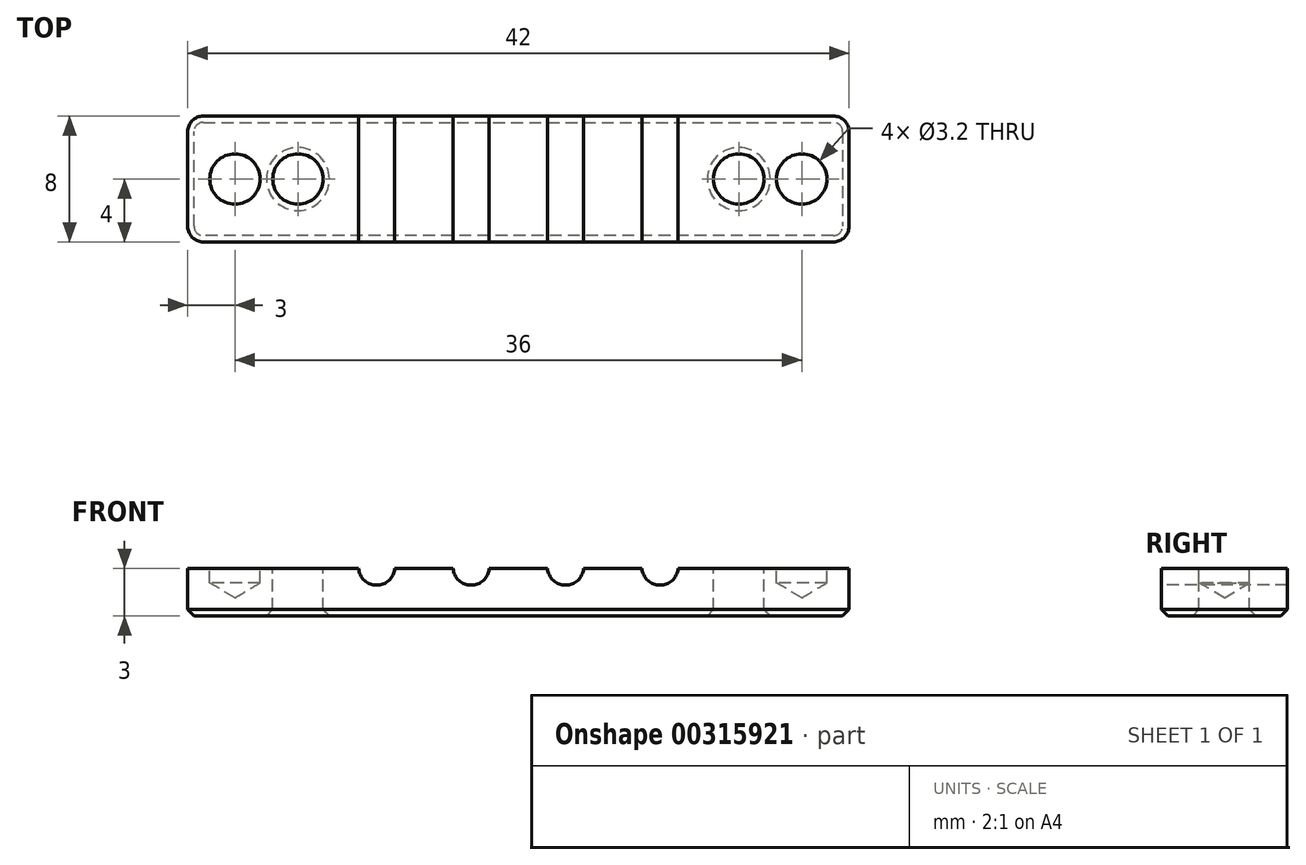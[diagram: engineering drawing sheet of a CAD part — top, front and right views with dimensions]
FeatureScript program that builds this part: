
annotation { "Feature Type Name" : "Feature", "Feature Type Description" : "" }
export const myFeature = defineFeature(function(context is Context, id is Id, definition is map)
    precondition{}
    {
        {
            var Q0;
            Q0=qCreatedBy(makeId("Top.planeOp"),FACE);
            var sketch = newSketch(context, id + "F0", { "sketchPlane" : qUnion([Q0])});
            skLineSegment(sketch, "E0.bottom", {"start": v(3, 4) * mm, "end": v(-3, 4) * mm});
            skLineSegment(sketch, "E0.top", {"start": v(3, -4) * mm, "end": v(-3, -4) * mm});
            skLineSegment(sketch, "E0.left", {"start": v(3, 4) * mm, "end": v(3, -4) * mm});
            skLineSegment(sketch, "E0.right", {"start": v(-3, 4) * mm, "end": v(-3, -4) * mm});
            skPoint(sketch, "E0.middle", {"position": v(0, 0) * mm});
            skLineSegment(sketch, "E1.bottom", {"start": v(39, 4) * mm, "end": v(33, 4) * mm});
            skLineSegment(sketch, "E1.top", {"start": v(39, -4) * mm, "end": v(33, -4) * mm});
            skLineSegment(sketch, "E1.left", {"start": v(39, 4) * mm, "end": v(39, -4) * mm});
            skLineSegment(sketch, "E1.right", {"start": v(33, 4) * mm, "end": v(33, -4) * mm});
            skPoint(sketch, "E1.middle", {"position": v(36, 0) * mm});
            skLineSegment(sketch, "E2", {"start": v(3, 4) * mm, "end": v(33, 4) * mm});
            skLineSegment(sketch, "E3", {"start": v(3, -4) * mm, "end": v(33, -4) * mm});
            skLineSegment(sketch, "E4", {"start": v(9, 4) * mm, "end": v(9, -4) * mm, "construction": true});
            skLineSegment(sketch, "E5.direction1", {"start": v(9, -4) * mm, "end": v(15, -4) * mm, "construction": true});
            skPoint(sketch, "E6", {"position": v(4, 0) * mm});
            skPoint(sketch, "E6.positionSnap0", {"position": v(3, 0) * mm});
            skPoint(sketch, "E7", {"position": v(32, 0) * mm});
            skPoint(sketch, "E7.positionSnap0", {"position": v(33, 0) * mm});
            skLineSegment(sketch, "E8.0.1.0", {"start": v(15, 4) * mm, "end": v(15, -4) * mm, "construction": true});
            skLineSegment(sketch, "E8.0.2.0", {"start": v(21, 4) * mm, "end": v(21, -4) * mm, "construction": true});
            skLineSegment(sketch, "E8.0.3.0", {"start": v(27, 4) * mm, "end": v(27, -4) * mm, "construction": true});
            skSolve(sketch);
        }
        {
            var Q0;
            Q0=makeQuery(id+"F0.imprint","IMPRINT",FACE,{"disambiguationData":[TD([[makeQuery(id+"F0.imprint","IMPRINT",EDGE,{"derivedFrom":sQuery(id+"F0.wireOp",EDGE,"E0.bottom")}),1.0]])]});
            var Q1;
            Q1=makeQuery(id+"F0.imprint","IMPRINT",FACE,{"disambiguationData":[TD([[makeQuery(id+"F0.imprint","IMPRINT",EDGE,{"derivedFrom":sQuery(id+"F0.wireOp",EDGE,"E0.left")}),1.0]])]});
            var Q2;
            Q2=makeQuery(id+"F0.imprint","IMPRINT",FACE,{"disambiguationData":[TD([[makeQuery(id+"F0.imprint","IMPRINT",EDGE,{"derivedFrom":sQuery(id+"F0.wireOp",EDGE,"E1.bottom")}),1.0]])]});
            extrude(context, id + "F1", {"entities" : qUnion([Q0, Q1, Q2]), "oppositeDirection" : true, "depth" : 3.1 * mm});
        }
        {
            var Q0;
            Q0=sQuery(id+"F0.wireOp",VERTEX,"E6");
            var Q1;
            Q1=sQuery(id+"F0.wireOp",VERTEX,"E7");
            var Q2;
            Q2=makeQuery(id+"F1.opExtrude","SWEPT_BODY",BODY,{"disambiguationData":[OSD([sQuery(id+"F0.wireOp",EDGE,"E0.bottom"),sQuery(id+"F0.wireOp",EDGE,"E0.top"),sQuery(id+"F0.wireOp",EDGE,"E0.right"),sQuery(id+"F0.wireOp",EDGE,"E1.bottom"),sQuery(id+"F0.wireOp",EDGE,"E1.top"),sQuery(id+"F0.wireOp",EDGE,"E1.left"),sQuery(id+"F0.wireOp",EDGE,"E2"),sQuery(id+"F0.wireOp",EDGE,"E3")])]});
            hole(context, id + "F2", {"style" : HoleStyle.SIMPLE, "endStyle" : HoleEndStyle.THROUGH, "holeDiameter" : 3.2 * mm, "tappedDepth" : 12 * mm, "tapClearance" : 3, "locations" : qUnion([Q0, Q1]), "scope" : qUnion([Q2])});
        }
        {
            var Q0;
            Q0=sQuery(id+"F0.wireOp",VERTEX,"E0.middle");
            var Q1;
            Q1=sQuery(id+"F0.wireOp",VERTEX,"E1.middle");
            var Q2;
            Q2=makeQuery(id+"F1.opExtrude","SWEPT_BODY",BODY,{"disambiguationData":[OSD([sQuery(id+"F0.wireOp",EDGE,"E0.bottom"),sQuery(id+"F0.wireOp",EDGE,"E0.top"),sQuery(id+"F0.wireOp",EDGE,"E0.right"),sQuery(id+"F0.wireOp",EDGE,"E1.bottom"),sQuery(id+"F0.wireOp",EDGE,"E1.top"),sQuery(id+"F0.wireOp",EDGE,"E1.left"),sQuery(id+"F0.wireOp",EDGE,"E2"),sQuery(id+"F0.wireOp",EDGE,"E3")])]});
            hole(context, id + "F3", {"style" : HoleStyle.SIMPLE, "endStyle" : HoleEndStyle.BLIND, "holeDiameter" : 3.2 * mm, "holeDepth" : 1 * mm, "tappedDepth" : 12 * mm, "tapClearance" : 3, "locations" : qUnion([Q0, Q1]), "scope" : qUnion([Q2])});
        }
        {
            var Q0;
            {var subQ0=sQuery(id+"F0.wireOp",EDGE,"E3");var subQ1=sQuery(id+"F0.wireOp",EDGE,"E1.top");var subQ2=sQuery(id+"F0.wireOp",EDGE,"E0.top");Q0=makeQuery(id+"FaaVOSY5iOmgxNq_1.boolean.opBoolean","MERGE",FACE,{"derivedFrom":[makeQuery(id+"F1.opExtrude","SWEPT_FACE",FACE,{"disambiguationData":[OSD([subQ2,subQ1,subQ0])]}),makeQuery(id+"FaaVOSY5iOmgxNq_1.opExtrude","SWEPT_FACE",FACE,{"disambiguationData":[OSD([subQ2,subQ1,subQ0])]})]});}
            var sketch = newSketch(context, id + "F4", { "sketchPlane" : qUnion([Q0])});
            skPoint(sketch, "E9", {"position": v(9, 0) * mm});
            skPoint(sketch, "E10.1.0.0", {"position": v(15, 0) * mm});
            skLineSegment(sketch, "E10.direction1", {"start": v(9, 0) * mm, "end": v(15, 0) * mm, "construction": true});
            skPoint(sketch, "E11.0.2.0", {"position": v(21, 0) * mm});
            skPoint(sketch, "E11.0.3.0", {"position": v(27, 0) * mm});
            skSolve(sketch);
        }
        {
            var Q0;
            Q0=sQuery(id+"F4.wireOp",VERTEX,"E9");
            var Q1;
            Q1=sQuery(id+"F4.wireOp",VERTEX,"E10.1.0.0");
            var Q2;
            Q2=sQuery(id+"F4.wireOp",VERTEX,"E11.0.2.0");
            var Q3;
            Q3=sQuery(id+"F4.wireOp",VERTEX,"E11.0.3.0");
            var Q4;
            Q4=makeQuery(id+"F1.opExtrude","SWEPT_BODY",BODY,{"disambiguationData":[OSD([sQuery(id+"F0.wireOp",EDGE,"E0.bottom"),sQuery(id+"F0.wireOp",EDGE,"E0.top"),sQuery(id+"F0.wireOp",EDGE,"E0.right"),sQuery(id+"F0.wireOp",EDGE,"E1.bottom"),sQuery(id+"F0.wireOp",EDGE,"E1.top"),sQuery(id+"F0.wireOp",EDGE,"E1.left"),sQuery(id+"F0.wireOp",EDGE,"E2"),sQuery(id+"F0.wireOp",EDGE,"E3")])]});
            hole(context, id + "F5", {"style" : HoleStyle.SIMPLE, "endStyle" : HoleEndStyle.THROUGH, "holeDiameter" : 2.3 * mm, "tappedDepth" : 12 * mm, "tapClearance" : 3, "locations" : qUnion([Q0, Q1, Q2, Q3]), "scope" : qUnion([Q4])});
        }
        {
            var Q0;
            Q0=makeQuery(id+"F1.opExtrude","SWEPT_EDGE",EDGE,{"disambiguationData":[OSD([sQuery(id+"F0.wireOp",EDGE,"E0.top"),sQuery(id+"F0.wireOp",EDGE,"E0.right")])]});
            var Q1;
            Q1=makeQuery(id+"F1.opExtrude","SWEPT_EDGE",EDGE,{"disambiguationData":[OSD([sQuery(id+"F0.wireOp",EDGE,"E1.top"),sQuery(id+"F0.wireOp",EDGE,"E1.left")])]});
            var Q2;
            Q2=makeQuery(id+"F1.opExtrude","SWEPT_EDGE",EDGE,{"disambiguationData":[OSD([sQuery(id+"F0.wireOp",EDGE,"E1.bottom"),sQuery(id+"F0.wireOp",EDGE,"E1.left")])]});
            var Q3;
            Q3=makeQuery(id+"F1.opExtrude","SWEPT_EDGE",EDGE,{"disambiguationData":[OSD([sQuery(id+"F0.wireOp",EDGE,"E0.bottom"),sQuery(id+"F0.wireOp",EDGE,"E0.right")])]});
            fillet(context, id + "F6", {"entities" : qUnion([Q0, Q1, Q2, Q3]), "radius" : 1 * mm, "tangentPropagation" : true, "allowEdgeOverflow" : false});
        }
        {
            var Q0;
            Q0=makeQuery(id+"F1.opExtrude","CAP_FACE",FACE,{"disambiguationData":[OSD([sQuery(id+"F0.wireOp",EDGE,"E0.bottom"),sQuery(id+"F0.wireOp",EDGE,"E0.top"),sQuery(id+"F0.wireOp",EDGE,"E0.right"),sQuery(id+"F0.wireOp",EDGE,"E1.bottom"),sQuery(id+"F0.wireOp",EDGE,"E1.top"),sQuery(id+"F0.wireOp",EDGE,"E1.left"),sQuery(id+"F0.wireOp",EDGE,"E2"),sQuery(id+"F0.wireOp",EDGE,"E3")])],"isStart":false});
            chamfer(context, id + "F7", {"entities" : qUnion([Q0]), "width" : 0.4 * mm, "tangentPropagation" : true});
        }
        {
            var Q0;
            {var subQ0=sQuery(id+"F0.wireOp",EDGE,"E0.right");var subQ1=sQuery(id+"F0.wireOp",EDGE,"E3");var subQ2=sQuery(id+"F0.wireOp",EDGE,"E1.top");var subQ3=sQuery(id+"F0.wireOp",EDGE,"E0.top");var subQ4=sQuery(id+"F0.wireOp",EDGE,"E2");var subQ5=sQuery(id+"F0.wireOp",EDGE,"E1.bottom");var subQ6=sQuery(id+"F0.wireOp",EDGE,"E0.bottom");Q0=makeQuery(id+"F5.hole-0.boolean.opBoolean","SPLIT",FACE,{"disambiguationData":[TD([makeQuery(id+"F1.opExtrude","SWEPT_FACE",FACE,{"disambiguationData":[OSD([subQ0])]})])],"derivedFrom":makeQuery(id+"F1.opExtrude","CAP_FACE",FACE,{"disambiguationData":[OSD([subQ6,subQ3,subQ0,subQ5,subQ2,sQuery(id+"F0.wireOp",EDGE,"E1.left"),subQ4,subQ1])],"isStart":true})});}
            var Q1;
            {var subQ0=sQuery(id+"F0.wireOp",EDGE,"E2");var subQ1=sQuery(id+"F0.wireOp",EDGE,"E1.bottom");var subQ2=sQuery(id+"F0.wireOp",EDGE,"E0.bottom");var subQ4=sQuery(id+"F0.wireOp",EDGE,"E3");var subQ5=sQuery(id+"F0.wireOp",EDGE,"E1.top");var subQ6=sQuery(id+"F0.wireOp",EDGE,"E0.top");var subQ8=makeQuery(id+"F5.hole-0.opRevolve","SWEPT_FACE",FACE,{"disambiguationData":[OSD([sQuery(id+"F5.hole-0.sketch.wireOp",EDGE,"core_line_2")])]});var subQ9=makeQuery(id+"F5.hole-0.boolean.opBoolean","COPY",FACE,{"derivedFrom":subQ8});var subQ10=sQuery(id+"F0.wireOp",EDGE,"E1.left");Q1=makeQuery(id+"F5.hole-2.boolean.opBoolean","SPLIT",FACE,{"disambiguationData":[TD([subQ9])],"derivedFrom":makeQuery(id+"F5.hole-1.boolean.opBoolean","SPLIT",FACE,{"disambiguationData":[TD([subQ9])],"derivedFrom":makeQuery(id+"F5.hole-0.boolean.opBoolean","SPLIT",FACE,{"disambiguationData":[TD([makeQuery(id+"F1.opExtrude","SWEPT_FACE",FACE,{"disambiguationData":[OSD([subQ10])]})])],"derivedFrom":makeQuery(id+"F1.opExtrude","CAP_FACE",FACE,{"disambiguationData":[OSD([subQ2,subQ6,sQuery(id+"F0.wireOp",EDGE,"E0.right"),subQ1,subQ5,subQ10,subQ0,subQ4])],"isStart":true})})})});}
            var Q2;
            {var subQ0=sQuery(id+"F0.wireOp",EDGE,"E2");var subQ1=sQuery(id+"F0.wireOp",EDGE,"E1.bottom");var subQ2=sQuery(id+"F0.wireOp",EDGE,"E0.bottom");var subQ4=sQuery(id+"F0.wireOp",EDGE,"E3");var subQ5=sQuery(id+"F0.wireOp",EDGE,"E1.top");var subQ6=sQuery(id+"F0.wireOp",EDGE,"E0.top");var subQ8=makeQuery(id+"F5.hole-1.opRevolve","SWEPT_FACE",FACE,{"disambiguationData":[OSD([sQuery(id+"F5.hole-1.sketch.wireOp",EDGE,"core_line_2")])]});var subQ9=makeQuery(id+"F5.hole-0.opRevolve","SWEPT_FACE",FACE,{"disambiguationData":[OSD([sQuery(id+"F5.hole-0.sketch.wireOp",EDGE,"core_line_2")])]});var subQ10=sQuery(id+"F0.wireOp",EDGE,"E1.left");Q2=makeQuery(id+"F5.hole-2.boolean.opBoolean","SPLIT",FACE,{"disambiguationData":[TD([makeQuery(id+"F5.hole-1.boolean.opBoolean","COPY",FACE,{"derivedFrom":subQ8})])],"derivedFrom":makeQuery(id+"F5.hole-1.boolean.opBoolean","SPLIT",FACE,{"disambiguationData":[TD([makeQuery(id+"F5.hole-0.boolean.opBoolean","COPY",FACE,{"derivedFrom":subQ9})])],"derivedFrom":makeQuery(id+"F5.hole-0.boolean.opBoolean","SPLIT",FACE,{"disambiguationData":[TD([makeQuery(id+"F1.opExtrude","SWEPT_FACE",FACE,{"disambiguationData":[OSD([subQ10])]})])],"derivedFrom":makeQuery(id+"F1.opExtrude","CAP_FACE",FACE,{"disambiguationData":[OSD([subQ2,subQ6,sQuery(id+"F0.wireOp",EDGE,"E0.right"),subQ1,subQ5,subQ10,subQ0,subQ4])],"isStart":true})})})});}
            var Q3;
            {var subQ1=sQuery(id+"F0.wireOp",EDGE,"E3");var subQ2=sQuery(id+"F0.wireOp",EDGE,"E1.top");var subQ3=sQuery(id+"F0.wireOp",EDGE,"E0.top");var subQ5=sQuery(id+"F0.wireOp",EDGE,"E1.left");var subQ6=makeQuery(id+"F1.opExtrude","SWEPT_FACE",FACE,{"disambiguationData":[OSD([subQ5])]});var subQ7=sQuery(id+"F0.wireOp",EDGE,"E2");var subQ8=sQuery(id+"F0.wireOp",EDGE,"E1.bottom");var subQ9=sQuery(id+"F0.wireOp",EDGE,"E0.bottom");Q3=makeQuery(id+"F5.hole-1.boolean.opBoolean","SPLIT",FACE,{"disambiguationData":[TD([subQ6])],"derivedFrom":makeQuery(id+"F5.hole-0.boolean.opBoolean","SPLIT",FACE,{"disambiguationData":[TD([subQ6])],"derivedFrom":makeQuery(id+"F1.opExtrude","CAP_FACE",FACE,{"disambiguationData":[OSD([subQ9,subQ3,sQuery(id+"F0.wireOp",EDGE,"E0.right"),subQ8,subQ2,subQ5,subQ7,subQ1])],"isStart":true})})});}
            extrude(context, id + "F8", {"entities" : qUnion([Q0, Q1, Q2, Q3]), "operationType" : NewBodyOperationType.REMOVE, "oppositeDirection" : true, "depth" : 0.1 * mm});
        }
    });
